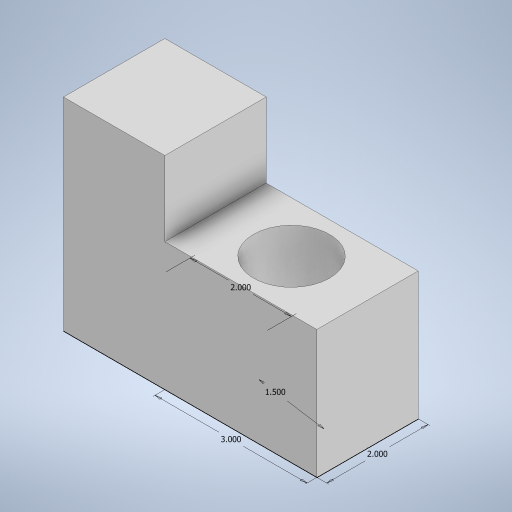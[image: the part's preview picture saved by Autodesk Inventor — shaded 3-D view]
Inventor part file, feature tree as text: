
AUTODESK INVENTOR PART (.ipt)
format: ipt  version: 2023 (Build 270158000, 158)  size: 218,624 bytes
history: native  units: in
note: dims shown in document units (in); Inventor stores cm internally (conversion verified against a paired STEP export)
features: extrude x2, sketch x1, mirror x1
ambient origin geometry x8: Origin, YZ Plane, XZ Plane, XY Plane, X Axis, Y Axis, Z Axis, Center Point
bodies: Solid1 (feature_tree)
feature tree (4):
  sketch  "Sketch1"  dims[d0=3.0in d1=2.0in d2=2.0in d3=1.5in d11=2.528in d12=0.0in d13=4.0in d14=0.0in]
  extrude  "Extrusion3"  Depth=2.0in
  extrude  "Extrusion4"  Depth=2.0in
  mirror  "Mirror1"
